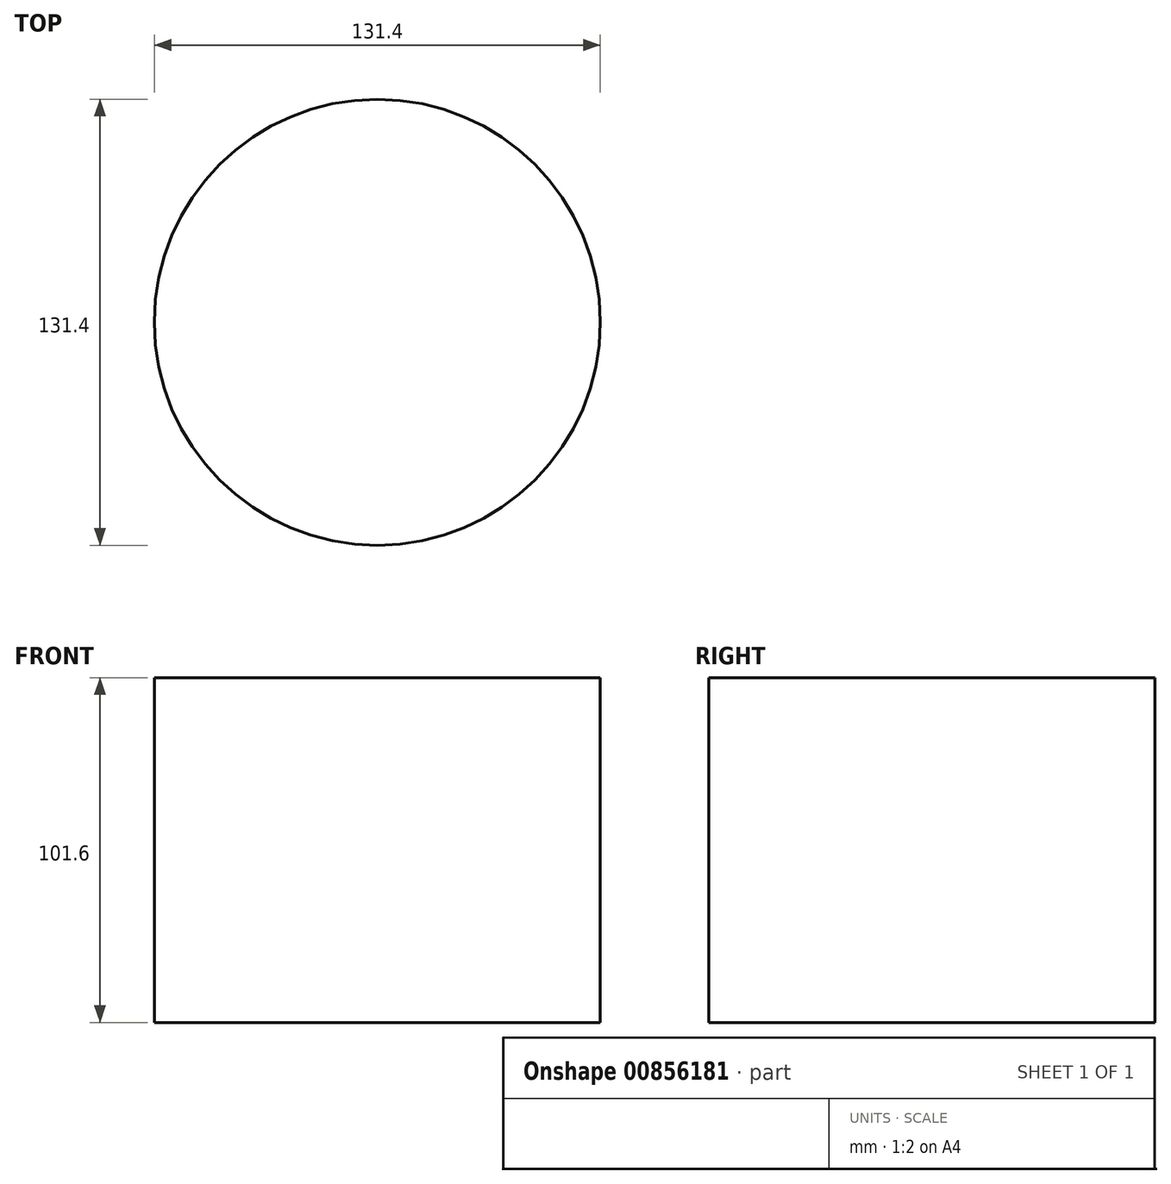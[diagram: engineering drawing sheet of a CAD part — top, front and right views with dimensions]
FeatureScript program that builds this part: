
annotation { "Feature Type Name" : "Feature", "Feature Type Description" : "" }
export const myFeature = defineFeature(function(context is Context, id is Id, definition is map)
    precondition{}
    {
        {
            var Q0;
            Q0=qCreatedBy(makeId("Top.planeOp"),FACE);
            var sketch = newSketch(context, id + "F0", { "sketchPlane" : qUnion([Q0])});
            skCircle(sketch, "E0", {"center": v(0, 0) * mm, "radius": 65.7 * mm});
            skSolve(sketch);
        }
        {
            var Q0;
            Q0 = qSketchRegion(id + "F0", true);
            extrude(context, id + "F1", {"entities" : qUnion([Q0]), "depth" : 101.6 * mm, "offsetDistance" : 25.4 * mm});
        }
    });
